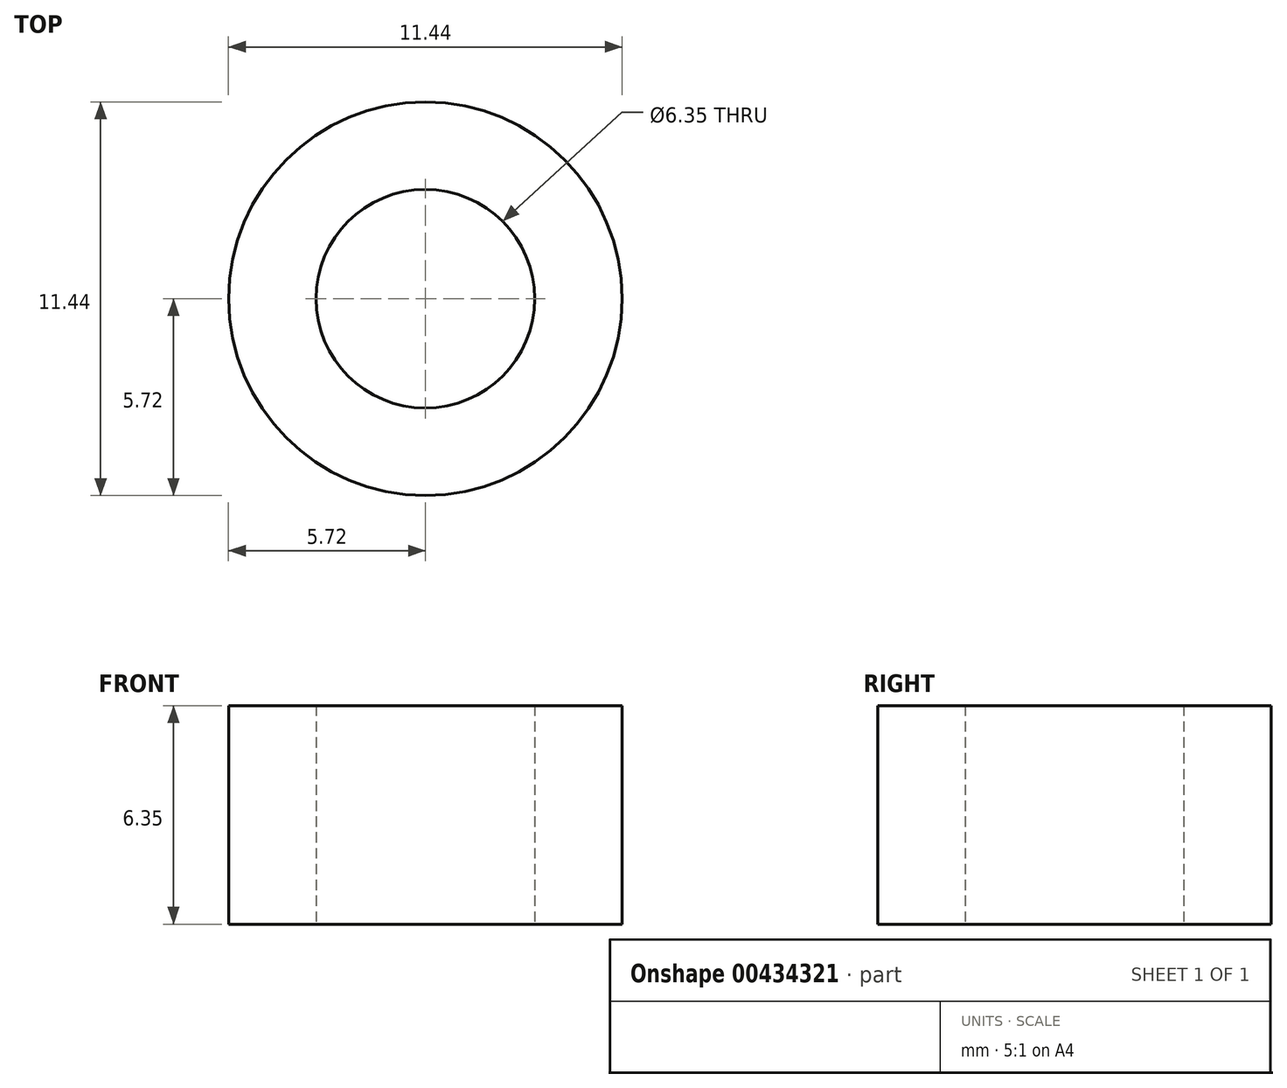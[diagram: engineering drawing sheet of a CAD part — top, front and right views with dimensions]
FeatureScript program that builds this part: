
annotation { "Feature Type Name" : "Feature", "Feature Type Description" : "" }
export const myFeature = defineFeature(function(context is Context, id is Id, definition is map)
    precondition{}
    {
        {
            var Q0;
            Q0=qCreatedBy(makeId("Top.planeOp"),FACE);
            var sketch = newSketch(context, id + "F0", { "sketchPlane" : qUnion([Q0])});
            skCircle(sketch, "E0", {"center": v(0, 0) * mm, "radius": 3.18 * mm});
            skCircle(sketch, "E1", {"center": v(0, 0) * mm, "radius": 5.72 * mm});
            skSolve(sketch);
        }
        {
            var Q0;
            Q0=qSketchRegion(id+"F0",true);
            extrude(context, id + "F1", {"entities" : qUnion([Q0]), "depth" : 6.35 * mm});
        }
    });
